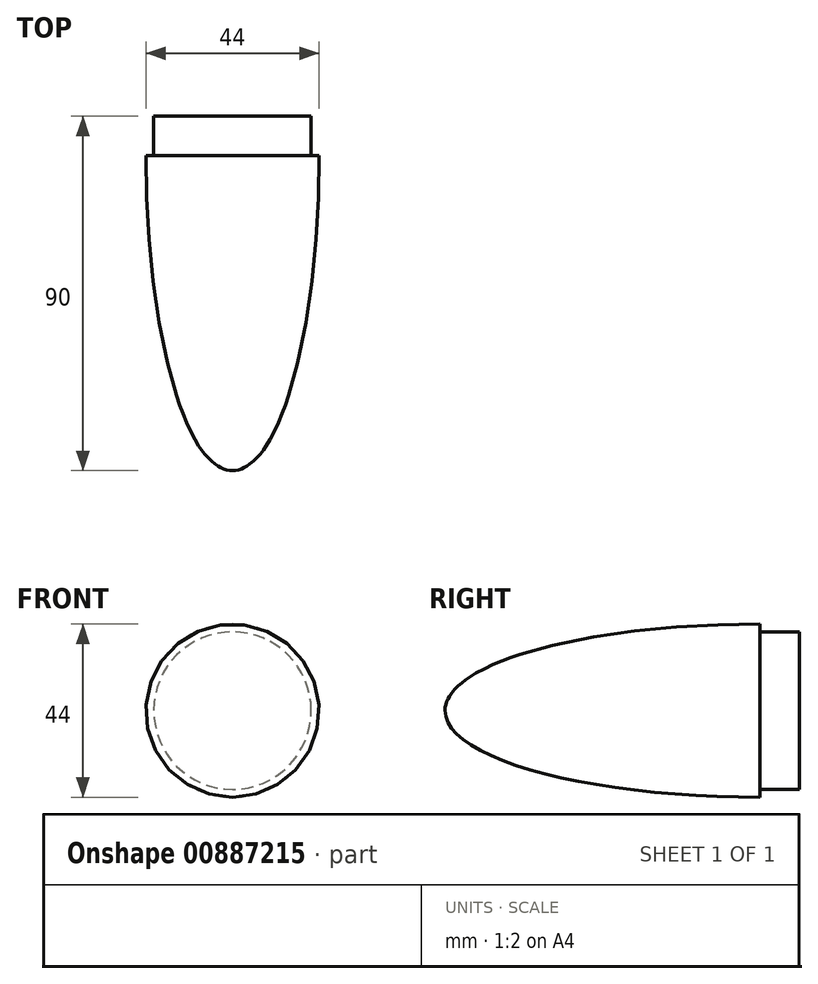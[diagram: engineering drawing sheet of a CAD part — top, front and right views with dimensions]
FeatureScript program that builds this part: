
annotation { "Feature Type Name" : "Feature", "Feature Type Description" : "" }
export const myFeature = defineFeature(function(context is Context, id is Id, definition is map)
    precondition{}
    {
        {
            var Q0;
            Q0=qCreatedBy(makeId("Right.planeOp"),FACE);
            var sketch = newSketch(context, id + "F0", { "sketchPlane" : qUnion([Q0])});
            skLineSegment(sketch, "E0.bottom", {"start": v(0, 0) * mm, "end": v(10, 0) * mm});
            skLineSegment(sketch, "E0.top", {"start": v(0, -20) * mm, "end": v(10, -20) * mm});
            skLineSegment(sketch, "E0.left", {"start": v(0, 0) * mm, "end": v(0, -20) * mm});
            skLineSegment(sketch, "E0.right", {"start": v(10, 0) * mm, "end": v(10, -20) * mm});
            skLineSegment(sketch, "E1.bottom", {"start": v(0, 0) * mm, "end": v(-80, 0) * mm});
            skLineSegment(sketch, "E1.top", {"start": v(0, -22) * mm, "end": v(-80, -22) * mm});
            skLineSegment(sketch, "E1.left", {"start": v(0, 0) * mm, "end": v(0, -22) * mm});
            skLineSegment(sketch, "E1.right", {"start": v(-80, 0) * mm, "end": v(-80, -22) * mm});
            skEllipse(sketch, "E2", {"center": v(0, 0) * mm, "majorRadius": 80 * mm, "minorRadius": 22 * mm, "majorAxis": v(-1, 0)});
            skSolve(sketch);
        }
        {
            var Q0;
            {var subQ0=sQuery(id+"F0.wireOp",EDGE,"E1.bottom");Q0=makeQuery(id+"F0.imprint","IMPRINT",FACE,{"disambiguationData":[TD([[makeQuery(id+"F0.imprint","IMPRINT",EDGE,{"derivedFrom":subQ0}),1.0]])]});}
            var Q1;
            {var subQ0=sQuery(id+"F0.wireOp",EDGE,"E0.bottom");Q1=makeQuery(id+"F0.imprint","IMPRINT",FACE,{"disambiguationData":[TD([[makeQuery(id+"F0.imprint","IMPRINT",EDGE,{"derivedFrom":subQ0}),-1.0]])]});}
            var Q2;
            Q2=sQuery(id+"F0.wireOp",EDGE,"E1.bottom");
            revolve(context, id + "F1", {"entities" : qUnion([Q0, Q1]), "axis" : qUnion([Q2]), "revolveType" : RevolveType.FULL});
        }
    });
